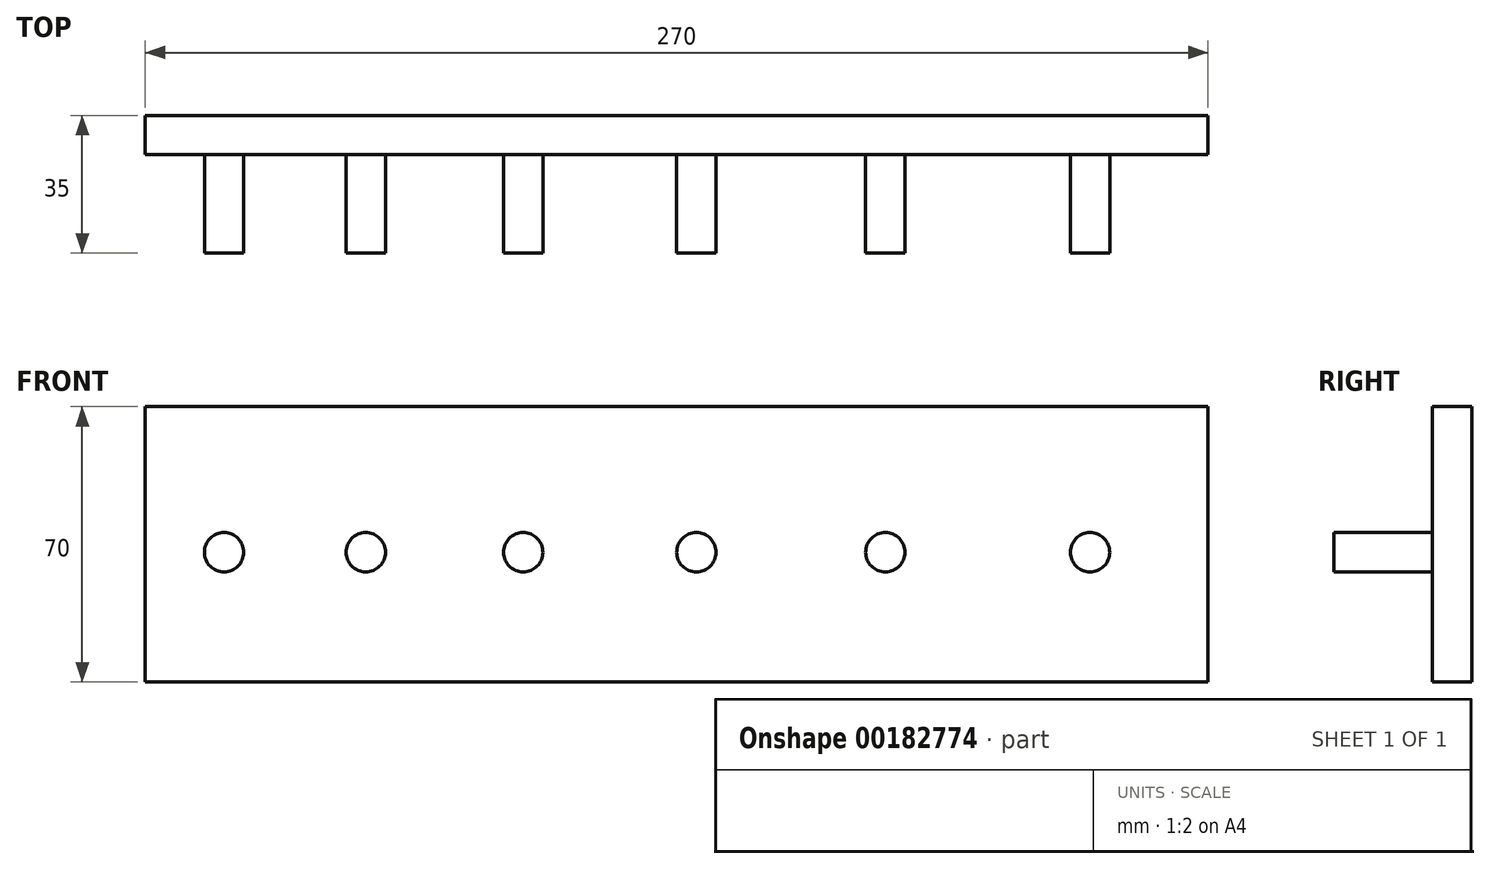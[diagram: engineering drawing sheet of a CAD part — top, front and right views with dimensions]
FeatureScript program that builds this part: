
annotation { "Feature Type Name" : "Feature", "Feature Type Description" : "" }
export const myFeature = defineFeature(function(context is Context, id is Id, definition is map)
    precondition{}
    {
        {
            var Q0;
            Q0=qCreatedBy(makeId("Front.planeOp"),FACE);
            var sketch = newSketch(context, id + "F0", { "sketchPlane" : qUnion([Q0])});
            skLineSegment(sketch, "E0.bottom", {"start": v(-146.4, 36.2) * mm, "end": v(123.6, 36.2) * mm});
            skLineSegment(sketch, "E0.top", {"start": v(-146.4, -33.8) * mm, "end": v(123.6, -33.8) * mm});
            skLineSegment(sketch, "E0.left", {"start": v(-146.4, 36.2) * mm, "end": v(-146.4, -33.8) * mm});
            skLineSegment(sketch, "E0.right", {"start": v(123.6, 36.2) * mm, "end": v(123.6, -33.8) * mm});
            skCircle(sketch, "E1", {"center": v(-126.4, 0) * mm, "radius": 5 * mm});
            skCircle(sketch, "E2", {"center": v(-90.4, 0) * mm, "radius": 5 * mm});
            skCircle(sketch, "E3", {"center": v(41.6, 0) * mm, "radius": 5 * mm});
            skCircle(sketch, "E4", {"center": v(-50.4, 0) * mm, "radius": 5 * mm});
            skCircle(sketch, "E5", {"center": v(93.6, 0) * mm, "radius": 5 * mm});
            skCircle(sketch, "E6", {"center": v(-6.4, 0) * mm, "radius": 5 * mm});
            skSolve(sketch);
        }
        {
            var Q0;
            Q0=makeQuery(id+"F0.imprint","IMPRINT",FACE,{"disambiguationData":[TD([[makeQuery(id+"F0.imprint","IMPRINT",EDGE,{"derivedFrom":sQuery(id+"F0.wireOp",EDGE,"E0.bottom")}),-1.0]])]});
            var Q1;
            Q1=makeQuery(id+"F0.imprint","IMPRINT",FACE,{"disambiguationData":[TD([[makeQuery(id+"F0.imprint","IMPRINT",EDGE,{"derivedFrom":sQuery(id+"F0.wireOp",EDGE,"E5")}),1.0]])]});
            var Q2;
            Q2=makeQuery(id+"F0.imprint","IMPRINT",FACE,{"disambiguationData":[TD([[makeQuery(id+"F0.imprint","IMPRINT",EDGE,{"derivedFrom":sQuery(id+"F0.wireOp",EDGE,"E3")}),1.0]])]});
            var Q3;
            Q3=makeQuery(id+"F0.imprint","IMPRINT",FACE,{"disambiguationData":[TD([[makeQuery(id+"F0.imprint","IMPRINT",EDGE,{"derivedFrom":sQuery(id+"F0.wireOp",EDGE,"E6")}),1.0]])]});
            var Q4;
            Q4=makeQuery(id+"F0.imprint","IMPRINT",FACE,{"disambiguationData":[TD([[makeQuery(id+"F0.imprint","IMPRINT",EDGE,{"derivedFrom":sQuery(id+"F0.wireOp",EDGE,"E4")}),1.0]])]});
            var Q5;
            Q5=makeQuery(id+"F0.imprint","IMPRINT",FACE,{"disambiguationData":[TD([[makeQuery(id+"F0.imprint","IMPRINT",EDGE,{"derivedFrom":sQuery(id+"F0.wireOp",EDGE,"E2")}),1.0]])]});
            var Q6;
            Q6=makeQuery(id+"F0.imprint","IMPRINT",FACE,{"disambiguationData":[TD([[makeQuery(id+"F0.imprint","IMPRINT",EDGE,{"derivedFrom":sQuery(id+"F0.wireOp",EDGE,"E1")}),1.0]])]});
            extrude(context, id + "F1", {"entities" : qUnion([Q0, Q1, Q2, Q3, Q4, Q5, Q6]), "depth" : 10 * mm});
        }
        {
            var Q0;
            Q0=makeQuery(id+"F1.opExtrude","CAP_FACE",FACE,{"disambiguationData":[OSD([sQuery(id+"F0.wireOp",EDGE,"E0.bottom"),sQuery(id+"F0.wireOp",EDGE,"E0.top"),sQuery(id+"F0.wireOp",EDGE,"E0.left"),sQuery(id+"F0.wireOp",EDGE,"E0.right"),sQuery(id+"F0.wireOp",EDGE,"E1"),sQuery(id+"F0.wireOp",EDGE,"E2"),sQuery(id+"F0.wireOp",EDGE,"E3"),sQuery(id+"F0.wireOp",EDGE,"E4"),sQuery(id+"F0.wireOp",EDGE,"E5"),sQuery(id+"F0.wireOp",EDGE,"E6")])],"isStart":false});
            var sketch = newSketch(context, id + "F2", { "sketchPlane" : qUnion([Q0])});
            skCircle(sketch, "E7", {"center": v(-90.4, -0.8) * mm, "radius": 5 * mm});
            skCircle(sketch, "E8", {"center": v(-50.4, -0.8) * mm, "radius": 5 * mm});
            skCircle(sketch, "E9", {"center": v(-6.4, -0.8) * mm, "radius": 5 * mm});
            skCircle(sketch, "E10", {"center": v(41.6, -0.8) * mm, "radius": 5 * mm});
            skCircle(sketch, "E11", {"center": v(93.6, -0.8) * mm, "radius": 5 * mm});
            skCircle(sketch, "E12", {"center": v(-126.4, -0.8) * mm, "radius": 5 * mm});
            skSolve(sketch);
        }
        {
            var Q0;
            Q0=makeQuery(id+"F2.imprint","IMPRINT",FACE,{"disambiguationData":[TD([[makeQuery(id+"F2.imprint","IMPRINT",EDGE,{"derivedFrom":sQuery(id+"F2.wireOp",EDGE,"E12")}),1.0]])]});
            var Q1;
            Q1=makeQuery(id+"F2.imprint","IMPRINT",FACE,{"disambiguationData":[TD([[makeQuery(id+"F2.imprint","IMPRINT",EDGE,{"derivedFrom":sQuery(id+"F2.wireOp",EDGE,"E7")}),1.0]])]});
            var Q2;
            Q2=makeQuery(id+"F2.imprint","IMPRINT",FACE,{"disambiguationData":[TD([[makeQuery(id+"F2.imprint","IMPRINT",EDGE,{"derivedFrom":sQuery(id+"F2.wireOp",EDGE,"E8")}),1.0]])]});
            var Q3;
            Q3=makeQuery(id+"F2.imprint","IMPRINT",FACE,{"disambiguationData":[TD([[makeQuery(id+"F2.imprint","IMPRINT",EDGE,{"derivedFrom":sQuery(id+"F2.wireOp",EDGE,"E10")}),1.0]])]});
            var Q4;
            Q4=makeQuery(id+"F2.imprint","IMPRINT",FACE,{"disambiguationData":[TD([[makeQuery(id+"F2.imprint","IMPRINT",EDGE,{"derivedFrom":sQuery(id+"F2.wireOp",EDGE,"E11")}),1.0]])]});
            var Q5;
            Q5=makeQuery(id+"F2.imprint","IMPRINT",FACE,{"disambiguationData":[TD([[makeQuery(id+"F2.imprint","IMPRINT",EDGE,{"derivedFrom":sQuery(id+"F2.wireOp",EDGE,"E9")}),1.0]])]});
            extrude(context, id + "F3", {"entities" : qUnion([Q0, Q1, Q2, Q3, Q4, Q5]), "operationType" : NewBodyOperationType.ADD, "depth" : 25 * mm});
        }
    });
